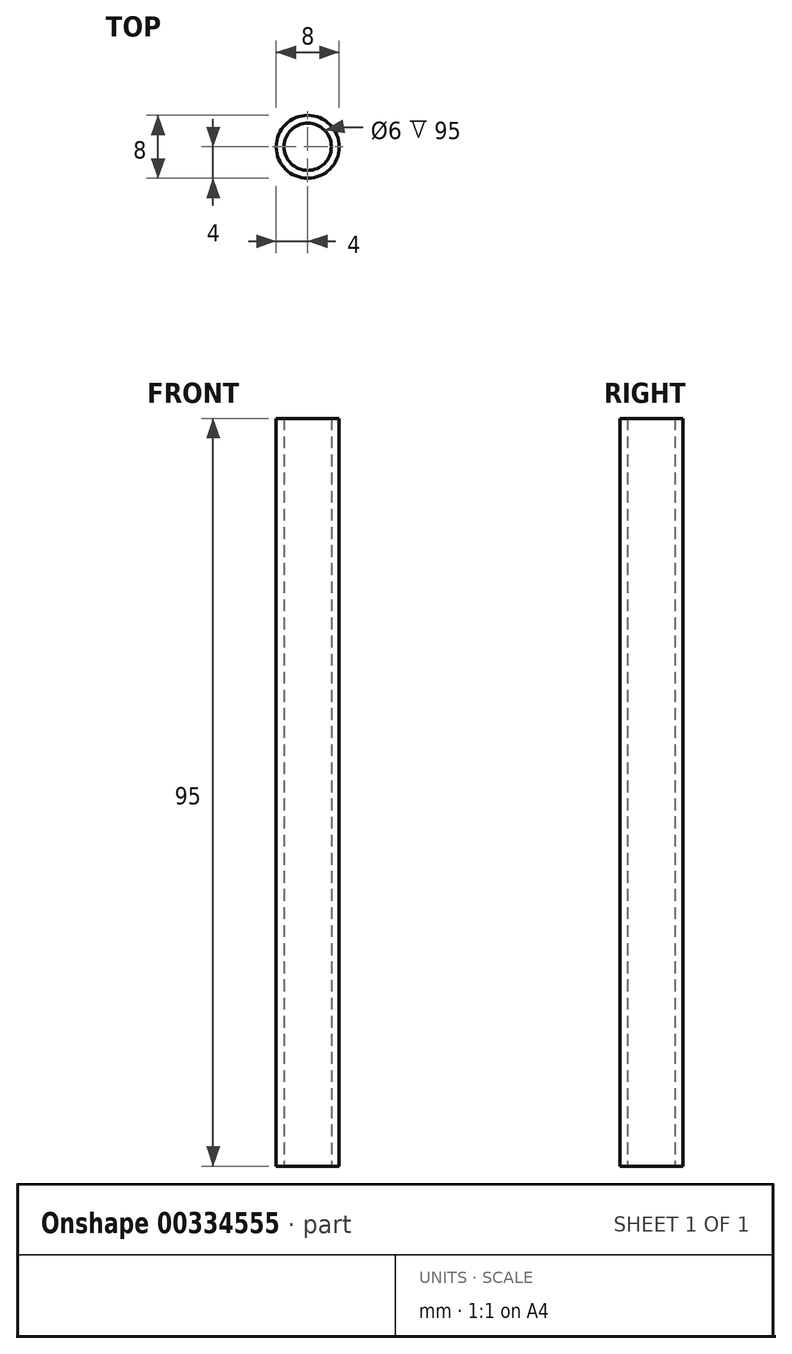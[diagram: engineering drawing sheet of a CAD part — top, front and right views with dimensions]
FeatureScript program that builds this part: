
annotation { "Feature Type Name" : "Feature", "Feature Type Description" : "" }
export const myFeature = defineFeature(function(context is Context, id is Id, definition is map)
    precondition{}
    {
        {
            var Q0;
            Q0=qCreatedBy(makeId("Top.planeOp"),FACE);
            var sketch = newSketch(context, id + "F0", { "sketchPlane" : qUnion([Q0])});
            skCircle(sketch, "E0", {"center": v(0, 0) * mm, "radius": 3 * mm});
            skCircle(sketch, "E1", {"center": v(0, 0) * mm, "radius": 4 * mm});
            skSolve(sketch);
        }
        {
            var Q0;
            Q0 = qSketchRegion(id + "F0", true);
            extrude(context, id + "F1", {"entities" : qUnion([Q0]), "depth" : 95 * mm});
        }
    });
